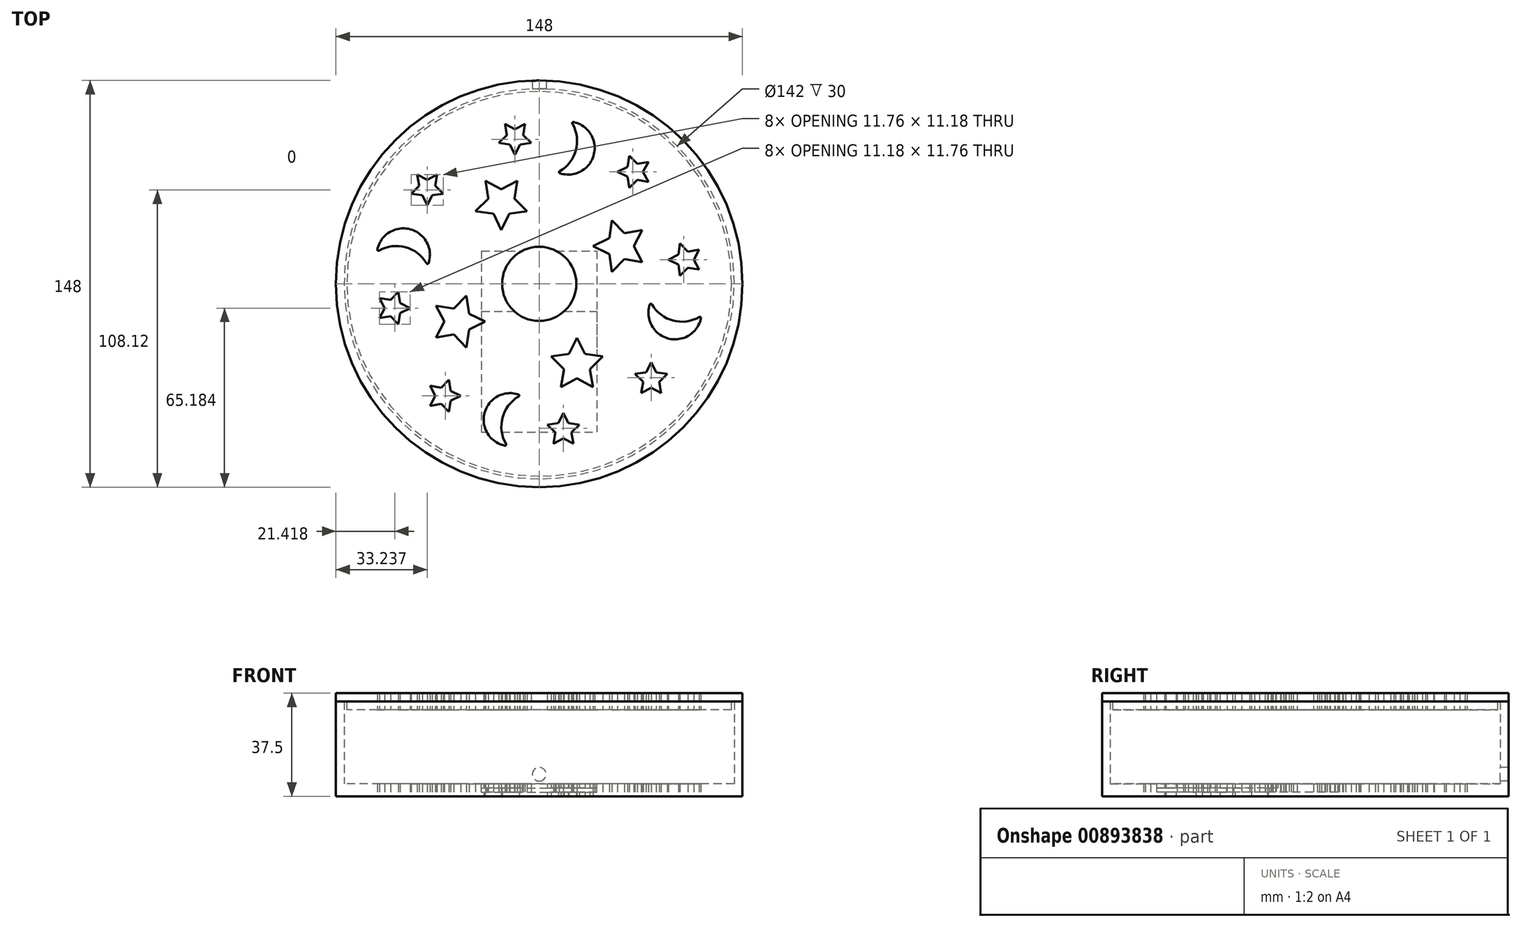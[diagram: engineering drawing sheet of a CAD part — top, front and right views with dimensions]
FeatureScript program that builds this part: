
annotation { "Feature Type Name" : "Feature", "Feature Type Description" : "" }
export const myFeature = defineFeature(function(context is Context, id is Id, definition is map)
    precondition{}
    {
        {
            assignVariable(context, id + "F0", {"name" : "BaseHeight", "anyValue" : 30});
        }
        {
            assignVariable(context, id + "F1", {"name" : "BaseThickness", "anyValue" : 4.5});
        }
        {
            assignVariable(context, id + "F2", {"name" : "CoverThickness", "anyValue" : 3});
        }
        {
            assignVariable(context, id + "F3", {"name" : "CoverLedge", "anyValue" : 3});
        }
        {
            var Q0;
            Q0=qCreatedBy(makeId("Top.planeOp"),FACE);
            var sketch = newSketch(context, id + "F4", { "sketchPlane" : qUnion([Q0])});
            skCircle(sketch, "E0", {"center": v(0, 0) * mm, "radius": 71 * mm});
            skCircle(sketch, "E1", {"center": v(0, 0) * mm, "radius": 74 * mm});
            skSolve(sketch);
        }
        {
            var Q0;
            Q0=makeQuery(id+"F4.imprint","IMPRINT",FACE,{"disambiguationData":[TD([[makeQuery(id+"F4.imprint","IMPRINT",EDGE,{"derivedFrom":sQuery(id+"F4.wireOp",EDGE,"E0")}),-1.0]])]});
            extrude(context, id + "F5", {"entities" : qUnion([Q0]), "depth" : (getVariable(context, 'BaseHeight') + getVariable(context, 'BaseThickness')) * mm, "offsetDistance" : 25 * mm});
        }
        {
            var Q0;
            Q0=makeQuery(id+"F4.imprint","IMPRINT",FACE,{"disambiguationData":[TD([[makeQuery(id+"F4.imprint","IMPRINT",EDGE,{"derivedFrom":sQuery(id+"F4.wireOp",EDGE,"E0")}),1.0]])]});
            extrude(context, id + "F6", {"entities" : qUnion([Q0]), "operationType" : NewBodyOperationType.ADD, "depth" : (getVariable(context, 'BaseThickness')) * mm, "offsetDistance" : 25 * mm});
        }
        {
            var Q0;
            Q0=qCreatedBy(makeId("Front.planeOp"),FACE);
            var sketch = newSketch(context, id + "F7", { "sketchPlane" : qUnion([Q0])});
            skLineSegment(sketch, "E2", {"start": v(0, 0) * mm, "end": v(0, 73.12) * mm, "construction": true});
            skSolve(sketch);
        }
        {
            var Q0;
            Q0=qCreatedBy(makeId("Front.planeOp"),FACE);
            var sketch = newSketch(context, id + "F8", { "sketchPlane" : qUnion([Q0])});
            skLineSegment(sketch, "E3.0.0", {"start": v(74, 0) * mm, "end": v(-74, 0) * mm});
            skLineSegment(sketch, "E4.0", {"start": v(-74, 34.5) * mm, "end": v(74, 34.5) * mm});
            skCircle(sketch, "E5", {"center": v(0, 8) * mm, "radius": 2.5 * mm});
            skSolve(sketch);
        }
        {
            var Q0;
            Q0=qSketchRegion(id+"F8",true);
            extrude(context, id + "F9", {"entities" : qUnion([Q0]), "operationType" : NewBodyOperationType.REMOVE, "endBound" : BoundingType.THROUGH_ALL, "oppositeDirection" : true, "depth" : 25 * mm, "offsetDistance" : 25 * mm});
        }
        {
            var Q0;
            Q0=qCreatedBy(makeId("Top.planeOp"),FACE);
            cPlane(context, id + "F10", {"entities" : qUnion([Q0]), "cplaneType" : CPlaneType.OFFSET, "offset" : (getVariable(context, 'BaseThickness')) * mm, "width" : 150 * mm, "height" : 150 * mm});
        }
        {
            var Q0;
            Q0=qCreatedBy(id+"F10.planeOp",FACE);
            var sketch = newSketch(context, id + "F11", { "sketchPlane" : qUnion([Q0])});
            skLineSegment(sketch, "E6.bottom", {"start": v(-21, 12) * mm, "end": v(21, 12) * mm});
            skLineSegment(sketch, "E6.top", {"start": v(-21, -54) * mm, "end": v(21, -54) * mm});
            skLineSegment(sketch, "E6.left", {"start": v(-21, 12) * mm, "end": v(-21, -54) * mm});
            skLineSegment(sketch, "E6.right", {"start": v(21, 12) * mm, "end": v(21, -54) * mm});
            skLineSegment(sketch, "E7", {"start": v(0, 35.82) * mm, "end": v(0, -36.35) * mm, "construction": true});
            skSolve(sketch);
        }
        {
            var Q0;
            Q0=qSketchRegion(id+"F11",true);
            extrude(context, id + "F12", {"entities" : qUnion([Q0]), "operationType" : NewBodyOperationType.REMOVE, "oppositeDirection" : true, "depth" : (getVariable(context, 'BaseThickness') - 1.5) * mm, "offsetDistance" : 25 * mm});
        }
        {
            var Q0;
            Q0=makeQuery(id+"F6.opExtrude","CAP_FACE",FACE,{"disambiguationData":[OSD([sQuery(id+"F4.wireOp",EDGE,"E0")])],"isStart":false});
            var sketch = newSketch(context, id + "F13", { "sketchPlane" : qUnion([Q0])});
            skLineSegment(sketch, "E8", {"start": v(-21, -10) * mm, "end": v(21, -10) * mm});
            skLineSegment(sketch, "E9", {"start": v(-21, -10) * mm, "end": v(-21, -54) * mm});
            skLineSegment(sketch, "E10", {"start": v(-21, -54) * mm, "end": v(21, -54) * mm});
            skLineSegment(sketch, "E11", {"start": v(21, -54) * mm, "end": v(21, -10) * mm});
            skSolve(sketch);
        }
        {
            var Q0;
            Q0=makeQuery(id+"F13.imprint","IMPRINT",FACE,{"disambiguationData":[TD([[makeQuery(id+"F13.imprint","IMPRINT",EDGE,{"derivedFrom":sQuery(id+"F13.wireOp",EDGE,"E8")}),-1.0]])]});
            extrude(context, id + "F14", {"entities" : qUnion([Q0]), "operationType" : NewBodyOperationType.ADD, "oppositeDirection" : true, "depth" : 1.5 * mm, "offsetDistance" : 25 * mm});
        }
        {
            var Q0;
            Q0=makeQuery(id+"F5.opExtrude","CAP_FACE",FACE,{"disambiguationData":[OSD([sQuery(id+"F4.wireOp",EDGE,"E0"),sQuery(id+"F4.wireOp",EDGE,"E1")])],"isStart":false});
            cPlane(context, id + "F15", {"entities" : qUnion([Q0]), "cplaneType" : CPlaneType.OFFSET, "offset" : 0 * mm, "width" : 150 * mm, "height" : 150 * mm});
        }
        {
            var Q0;
            Q0=qCreatedBy(id+"F15.planeOp",FACE);
            var sketch = newSketch(context, id + "F16", { "sketchPlane" : qUnion([Q0])});
            skCircle(sketch, "E12.0", {"center": v(0, 0) * mm, "radius": 74 * mm});
            skCircle(sketch, "E13.0", {"center": v(0, 0) * mm, "radius": 71 * mm});
            skCircle(sketch, "E14.0", {"center": v(0, 0) * mm, "radius": 70 * mm});
            skCircle(sketch, "E15.0", {"center": v(0, 0) * mm, "radius": 67 * mm});
            skSolve(sketch);
        }
        {
            var Q0;
            Q0=qSketchRegion(id+"F16",true);
            var Q1;
            Q1=makeQuery(id+"F16.imprint","IMPRINT",FACE,{"disambiguationData":[TD([[makeQuery(id+"F16.imprint","IMPRINT",EDGE,{"derivedFrom":sQuery(id+"F16.wireOp",EDGE,"E13.0")}),1.0]])]});
            var Q2;
            Q2=makeQuery(id+"F16.imprint","IMPRINT",FACE,{"disambiguationData":[TD([[makeQuery(id+"F16.imprint","IMPRINT",EDGE,{"derivedFrom":sQuery(id+"F16.wireOp",EDGE,"E14.0")}),1.0]])]});
            var Q3;
            Q3=makeQuery(id+"F16.imprint","IMPRINT",FACE,{"disambiguationData":[TD([[makeQuery(id+"F16.imprint","IMPRINT",EDGE,{"derivedFrom":sQuery(id+"F16.wireOp",EDGE,"E15.0")}),1.0]])]});
            extrude(context, id + "F17", {"entities" : qUnion([Q0, Q1, Q2, Q3]), "depth" : (getVariable(context, 'CoverThickness')) * mm, "offsetDistance" : 25 * mm});
        }
        {
            var Q0;
            Q0=makeQuery(id+"F16.imprint","IMPRINT",FACE,{"disambiguationData":[TD([[makeQuery(id+"F16.imprint","IMPRINT",EDGE,{"derivedFrom":sQuery(id+"F16.wireOp",EDGE,"E14.0")}),1.0]])]});
            var Q1;
            Q1=makeQuery(id+"F16.imprint","IMPRINT",FACE,{"disambiguationData":[TD([[makeQuery(id+"F16.imprint","IMPRINT",EDGE,{"derivedFrom":sQuery(id+"F16.wireOp",EDGE,"E15.0")}),1.0]])]});
            extrude(context, id + "F18", {"entities" : qUnion([Q0, Q1]), "operationType" : NewBodyOperationType.ADD, "oppositeDirection" : true, "depth" : (getVariable(context, 'CoverLedge')) * mm, "offsetDistance" : 25 * mm});
        }
        {
            var Q0;
            Q0=qCreatedBy(id+"F15.planeOp",FACE);
            var sketch = newSketch(context, id + "F19", { "sketchPlane" : qUnion([Q0])});
            skCircle(sketch, "E16", {"center": v(0, 0) * mm, "radius": 13.5 * mm});
            skPoint(sketch, "E17", {"position": v(34.71, 40.76) * mm});
            skLineSegment(sketch, "E18", {"start": v(28.53, 40.76) * mm, "end": v(32.21, 42.58) * mm});
            skLineSegment(sketch, "E19", {"start": v(32.21, 42.58) * mm, "end": v(32.8, 46.64) * mm});
            skLineSegment(sketch, "E20", {"start": v(32.8, 46.64) * mm, "end": v(35.67, 43.7) * mm});
            skLineSegment(sketch, "E21", {"start": v(35.67, 43.7) * mm, "end": v(39.71, 44.4) * mm});
            skLineSegment(sketch, "E22", {"start": v(39.71, 44.4) * mm, "end": v(37.8, 40.76) * mm});
            skLineSegment(sketch, "E23", {"start": v(37.8, 40.76) * mm, "end": v(39.71, 37.13) * mm});
            skLineSegment(sketch, "E24", {"start": v(39.71, 37.13) * mm, "end": v(35.67, 37.82) * mm});
            skLineSegment(sketch, "E25", {"start": v(35.67, 37.82) * mm, "end": v(32.8, 34.89) * mm});
            skLineSegment(sketch, "E26", {"start": v(32.8, 34.89) * mm, "end": v(32.21, 38.95) * mm});
            skLineSegment(sketch, "E27", {"start": v(32.21, 38.95) * mm, "end": v(28.53, 40.76) * mm});
            skPoint(sketch, "E28", {"position": v(53.17, 8.82) * mm});
            skLineSegment(sketch, "E29", {"start": v(47, 8.82) * mm, "end": v(50.67, 10.63) * mm});
            skLineSegment(sketch, "E30", {"start": v(50.67, 10.63) * mm, "end": v(51.26, 14.7) * mm});
            skLineSegment(sketch, "E31", {"start": v(51.26, 14.7) * mm, "end": v(54.13, 11.76) * mm});
            skLineSegment(sketch, "E32", {"start": v(54.13, 11.76) * mm, "end": v(58.17, 12.45) * mm});
            skLineSegment(sketch, "E33", {"start": v(58.17, 12.45) * mm, "end": v(56.26, 8.82) * mm});
            skLineSegment(sketch, "E34", {"start": v(56.26, 8.82) * mm, "end": v(58.17, 5.18) * mm});
            skLineSegment(sketch, "E35", {"start": v(58.17, 5.18) * mm, "end": v(54.13, 5.88) * mm});
            skLineSegment(sketch, "E36", {"start": v(54.13, 5.88) * mm, "end": v(51.26, 2.94) * mm});
            skLineSegment(sketch, "E37", {"start": v(51.26, 2.94) * mm, "end": v(50.67, 7) * mm});
            skLineSegment(sketch, "E38", {"start": v(50.67, 7) * mm, "end": v(47, 8.82) * mm});
            skLineSegment(sketch, "E39", {"start": v(19.63, 13.76) * mm, "end": v(25.52, 16.67) * mm});
            skLineSegment(sketch, "E40", {"start": v(25.52, 16.67) * mm, "end": v(26.46, 23.16) * mm});
            skLineSegment(sketch, "E41", {"start": v(26.46, 23.16) * mm, "end": v(31.05, 18.46) * mm});
            skLineSegment(sketch, "E42", {"start": v(31.05, 18.46) * mm, "end": v(37.52, 19.57) * mm});
            skLineSegment(sketch, "E43", {"start": v(37.52, 19.57) * mm, "end": v(34.46, 13.76) * mm});
            skLineSegment(sketch, "E44", {"start": v(34.46, 13.76) * mm, "end": v(37.52, 7.95) * mm});
            skLineSegment(sketch, "E45", {"start": v(37.52, 7.95) * mm, "end": v(31.05, 9.06) * mm});
            skLineSegment(sketch, "E46", {"start": v(31.05, 9.06) * mm, "end": v(26.46, 4.35) * mm});
            skLineSegment(sketch, "E47", {"start": v(26.46, 4.35) * mm, "end": v(25.52, 10.85) * mm});
            skLineSegment(sketch, "E48", {"start": v(25.52, 10.85) * mm, "end": v(19.63, 13.76) * mm});
            skArc(sketch, "E49", {"start": v(7.54, 40.26) * mm, "mid": v(19.88, 46.94) * mm, "end": v(12.5, 58.88) * mm});
            skArc(sketch, "E50", {"start": v(7.46, 41) * mm, "mid": v(13.35, 48.68) * mm, "end": v(12.08, 58.29) * mm});
            skPoint(sketch, "E51.visualSharp", {"position": v(11.62, 59.02) * mm});
            skArc(sketch, "E51.filletArc", {"start": v(12.5, 58.88) * mm, "mid": v(12.1, 58.72) * mm, "end": v(12.08, 58.29) * mm});
            skPoint(sketch, "E52.visualSharp", {"position": v(6.7, 40.58) * mm});
            skArc(sketch, "E52.filletArc", {"start": v(7.46, 41) * mm, "mid": v(7.27, 40.6) * mm, "end": v(7.54, 40.26) * mm});
            skArc(sketch, "E53.1.0", {"start": v(-40.26, 7.54) * mm, "mid": v(-46.94, 19.88) * mm, "end": v(-58.88, 12.5) * mm});
            skArc(sketch, "E53.1.1", {"start": v(-41, 7.46) * mm, "mid": v(-48.68, 13.35) * mm, "end": v(-58.29, 12.08) * mm});
            skLineSegment(sketch, "E53.1.2", {"start": v(-44.4, 39.71) * mm, "end": v(-40.76, 37.8) * mm});
            skPoint(sketch, "E53.1.3", {"position": v(-40.76, 34.71) * mm});
            skLineSegment(sketch, "E53.1.4", {"start": v(-46.64, 32.8) * mm, "end": v(-43.7, 35.67) * mm});
            skLineSegment(sketch, "E53.1.5", {"start": v(-37.13, 39.71) * mm, "end": v(-37.82, 35.67) * mm});
            skLineSegment(sketch, "E53.1.6", {"start": v(-38.95, 32.21) * mm, "end": v(-40.76, 28.53) * mm});
            skLineSegment(sketch, "E53.1.7", {"start": v(-37.82, 35.67) * mm, "end": v(-34.89, 32.8) * mm});
            skLineSegment(sketch, "E53.1.8", {"start": v(-40.76, 37.8) * mm, "end": v(-37.13, 39.71) * mm});
            skLineSegment(sketch, "E53.1.9", {"start": v(-42.58, 32.21) * mm, "end": v(-46.64, 32.8) * mm});
            skLineSegment(sketch, "E53.1.10", {"start": v(-43.7, 35.67) * mm, "end": v(-44.4, 39.71) * mm});
            skLineSegment(sketch, "E53.1.11", {"start": v(-40.76, 28.53) * mm, "end": v(-42.58, 32.21) * mm});
            skLineSegment(sketch, "E53.1.12", {"start": v(-34.89, 32.8) * mm, "end": v(-38.95, 32.21) * mm});
            skPoint(sketch, "E53.1.13", {"position": v(-8.82, 53.17) * mm});
            skLineSegment(sketch, "E53.1.14", {"start": v(-8.82, 56.26) * mm, "end": v(-5.18, 58.17) * mm});
            skLineSegment(sketch, "E53.1.15", {"start": v(-11.76, 54.13) * mm, "end": v(-12.45, 58.17) * mm});
            skLineSegment(sketch, "E53.1.16", {"start": v(-5.18, 58.17) * mm, "end": v(-5.88, 54.13) * mm});
            skLineSegment(sketch, "E53.1.17", {"start": v(-12.45, 58.17) * mm, "end": v(-8.82, 56.26) * mm});
            skLineSegment(sketch, "E53.1.18", {"start": v(-14.7, 51.26) * mm, "end": v(-11.76, 54.13) * mm});
            skLineSegment(sketch, "E53.1.19", {"start": v(-7, 50.67) * mm, "end": v(-8.82, 47) * mm});
            skLineSegment(sketch, "E53.1.20", {"start": v(-2.94, 51.26) * mm, "end": v(-7, 50.67) * mm});
            skLineSegment(sketch, "E53.1.21", {"start": v(-8.82, 47) * mm, "end": v(-10.63, 50.67) * mm});
            skLineSegment(sketch, "E53.1.22", {"start": v(-5.88, 54.13) * mm, "end": v(-2.94, 51.26) * mm});
            skLineSegment(sketch, "E53.1.23", {"start": v(-10.63, 50.67) * mm, "end": v(-14.7, 51.26) * mm});
            skLineSegment(sketch, "E53.1.24", {"start": v(-23.16, 26.46) * mm, "end": v(-18.46, 31.05) * mm});
            skLineSegment(sketch, "E53.1.25", {"start": v(-9.06, 31.05) * mm, "end": v(-4.35, 26.46) * mm});
            skLineSegment(sketch, "E53.1.26", {"start": v(-10.85, 25.52) * mm, "end": v(-13.76, 19.63) * mm});
            skLineSegment(sketch, "E53.1.27", {"start": v(-7.95, 37.52) * mm, "end": v(-9.06, 31.05) * mm});
            skLineSegment(sketch, "E53.1.28", {"start": v(-16.67, 25.52) * mm, "end": v(-23.16, 26.46) * mm});
            skLineSegment(sketch, "E53.1.29", {"start": v(-13.76, 34.46) * mm, "end": v(-7.95, 37.52) * mm});
            skLineSegment(sketch, "E53.1.30", {"start": v(-13.76, 19.63) * mm, "end": v(-16.67, 25.52) * mm});
            skLineSegment(sketch, "E53.1.31", {"start": v(-18.46, 31.05) * mm, "end": v(-19.57, 37.52) * mm});
            skLineSegment(sketch, "E53.1.32", {"start": v(-4.35, 26.46) * mm, "end": v(-10.85, 25.52) * mm});
            skLineSegment(sketch, "E53.1.33", {"start": v(-19.57, 37.52) * mm, "end": v(-13.76, 34.46) * mm});
            skArc(sketch, "E53.2.0", {"start": v(-7.54, -40.26) * mm, "mid": v(-19.88, -46.94) * mm, "end": v(-12.5, -58.88) * mm});
            skArc(sketch, "E53.2.1", {"start": v(-7.46, -41) * mm, "mid": v(-13.35, -48.68) * mm, "end": v(-12.08, -58.29) * mm});
            skLineSegment(sketch, "E53.2.2", {"start": v(-39.71, -44.4) * mm, "end": v(-37.8, -40.76) * mm});
            skPoint(sketch, "E53.2.3", {"position": v(-34.71, -40.76) * mm});
            skLineSegment(sketch, "E53.2.4", {"start": v(-32.8, -46.64) * mm, "end": v(-35.67, -43.7) * mm});
            skLineSegment(sketch, "E53.2.5", {"start": v(-39.71, -37.13) * mm, "end": v(-35.67, -37.82) * mm});
            skLineSegment(sketch, "E53.2.6", {"start": v(-32.21, -38.95) * mm, "end": v(-28.53, -40.76) * mm});
            skLineSegment(sketch, "E53.2.7", {"start": v(-35.67, -37.82) * mm, "end": v(-32.8, -34.89) * mm});
            skLineSegment(sketch, "E53.2.8", {"start": v(-37.8, -40.76) * mm, "end": v(-39.71, -37.13) * mm});
            skLineSegment(sketch, "E53.2.9", {"start": v(-32.21, -42.58) * mm, "end": v(-32.8, -46.64) * mm});
            skLineSegment(sketch, "E53.2.10", {"start": v(-35.67, -43.7) * mm, "end": v(-39.71, -44.4) * mm});
            skLineSegment(sketch, "E53.2.11", {"start": v(-28.53, -40.76) * mm, "end": v(-32.21, -42.58) * mm});
            skLineSegment(sketch, "E53.2.12", {"start": v(-32.8, -34.89) * mm, "end": v(-32.21, -38.95) * mm});
            skPoint(sketch, "E53.2.13", {"position": v(-53.17, -8.82) * mm});
            skLineSegment(sketch, "E53.2.14", {"start": v(-56.26, -8.82) * mm, "end": v(-58.17, -5.18) * mm});
            skLineSegment(sketch, "E53.2.15", {"start": v(-54.13, -11.76) * mm, "end": v(-58.17, -12.45) * mm});
            skLineSegment(sketch, "E53.2.16", {"start": v(-58.17, -5.18) * mm, "end": v(-54.13, -5.88) * mm});
            skLineSegment(sketch, "E53.2.17", {"start": v(-58.17, -12.45) * mm, "end": v(-56.26, -8.82) * mm});
            skLineSegment(sketch, "E53.2.18", {"start": v(-51.26, -14.7) * mm, "end": v(-54.13, -11.76) * mm});
            skLineSegment(sketch, "E53.2.19", {"start": v(-50.67, -7) * mm, "end": v(-47, -8.82) * mm});
            skLineSegment(sketch, "E53.2.20", {"start": v(-51.26, -2.94) * mm, "end": v(-50.67, -7) * mm});
            skLineSegment(sketch, "E53.2.21", {"start": v(-47, -8.82) * mm, "end": v(-50.67, -10.63) * mm});
            skLineSegment(sketch, "E53.2.22", {"start": v(-54.13, -5.88) * mm, "end": v(-51.26, -2.94) * mm});
            skLineSegment(sketch, "E53.2.23", {"start": v(-50.67, -10.63) * mm, "end": v(-51.26, -14.7) * mm});
            skLineSegment(sketch, "E53.2.24", {"start": v(-26.46, -23.16) * mm, "end": v(-31.05, -18.46) * mm});
            skLineSegment(sketch, "E53.2.25", {"start": v(-31.05, -9.06) * mm, "end": v(-26.46, -4.35) * mm});
            skLineSegment(sketch, "E53.2.26", {"start": v(-25.52, -10.85) * mm, "end": v(-19.63, -13.76) * mm});
            skLineSegment(sketch, "E53.2.27", {"start": v(-37.52, -7.95) * mm, "end": v(-31.05, -9.06) * mm});
            skLineSegment(sketch, "E53.2.28", {"start": v(-25.52, -16.67) * mm, "end": v(-26.46, -23.16) * mm});
            skLineSegment(sketch, "E53.2.29", {"start": v(-34.46, -13.76) * mm, "end": v(-37.52, -7.95) * mm});
            skLineSegment(sketch, "E53.2.30", {"start": v(-19.63, -13.76) * mm, "end": v(-25.52, -16.67) * mm});
            skLineSegment(sketch, "E53.2.31", {"start": v(-31.05, -18.46) * mm, "end": v(-37.52, -19.57) * mm});
            skLineSegment(sketch, "E53.2.32", {"start": v(-26.46, -4.35) * mm, "end": v(-25.52, -10.85) * mm});
            skLineSegment(sketch, "E53.2.33", {"start": v(-37.52, -19.57) * mm, "end": v(-34.46, -13.76) * mm});
            skArc(sketch, "E53.3.0", {"start": v(40.26, -7.54) * mm, "mid": v(46.94, -19.88) * mm, "end": v(58.88, -12.5) * mm});
            skArc(sketch, "E53.3.1", {"start": v(41, -7.46) * mm, "mid": v(48.68, -13.35) * mm, "end": v(58.29, -12.08) * mm});
            skLineSegment(sketch, "E53.3.2", {"start": v(44.4, -39.71) * mm, "end": v(40.76, -37.8) * mm});
            skPoint(sketch, "E53.3.3", {"position": v(40.76, -34.71) * mm});
            skLineSegment(sketch, "E53.3.4", {"start": v(46.64, -32.8) * mm, "end": v(43.7, -35.67) * mm});
            skLineSegment(sketch, "E53.3.5", {"start": v(37.13, -39.71) * mm, "end": v(37.82, -35.67) * mm});
            skLineSegment(sketch, "E53.3.6", {"start": v(38.95, -32.21) * mm, "end": v(40.76, -28.53) * mm});
            skLineSegment(sketch, "E53.3.7", {"start": v(37.82, -35.67) * mm, "end": v(34.89, -32.8) * mm});
            skLineSegment(sketch, "E53.3.8", {"start": v(40.76, -37.8) * mm, "end": v(37.13, -39.71) * mm});
            skLineSegment(sketch, "E53.3.9", {"start": v(42.58, -32.21) * mm, "end": v(46.64, -32.8) * mm});
            skLineSegment(sketch, "E53.3.10", {"start": v(43.7, -35.67) * mm, "end": v(44.4, -39.71) * mm});
            skLineSegment(sketch, "E53.3.11", {"start": v(40.76, -28.53) * mm, "end": v(42.58, -32.21) * mm});
            skLineSegment(sketch, "E53.3.12", {"start": v(34.89, -32.8) * mm, "end": v(38.95, -32.21) * mm});
            skPoint(sketch, "E53.3.13", {"position": v(8.82, -53.17) * mm});
            skLineSegment(sketch, "E53.3.14", {"start": v(8.82, -56.26) * mm, "end": v(5.18, -58.17) * mm});
            skLineSegment(sketch, "E53.3.15", {"start": v(11.76, -54.13) * mm, "end": v(12.45, -58.17) * mm});
            skLineSegment(sketch, "E53.3.16", {"start": v(5.18, -58.17) * mm, "end": v(5.88, -54.13) * mm});
            skLineSegment(sketch, "E53.3.17", {"start": v(12.45, -58.17) * mm, "end": v(8.82, -56.26) * mm});
            skLineSegment(sketch, "E53.3.18", {"start": v(14.7, -51.26) * mm, "end": v(11.76, -54.13) * mm});
            skLineSegment(sketch, "E53.3.19", {"start": v(7, -50.67) * mm, "end": v(8.82, -47) * mm});
            skLineSegment(sketch, "E53.3.20", {"start": v(2.94, -51.26) * mm, "end": v(7, -50.67) * mm});
            skLineSegment(sketch, "E53.3.21", {"start": v(8.82, -47) * mm, "end": v(10.63, -50.67) * mm});
            skLineSegment(sketch, "E53.3.22", {"start": v(5.88, -54.13) * mm, "end": v(2.94, -51.26) * mm});
            skLineSegment(sketch, "E53.3.23", {"start": v(10.63, -50.67) * mm, "end": v(14.7, -51.26) * mm});
            skLineSegment(sketch, "E53.3.24", {"start": v(23.16, -26.46) * mm, "end": v(18.46, -31.05) * mm});
            skLineSegment(sketch, "E53.3.25", {"start": v(9.06, -31.05) * mm, "end": v(4.35, -26.46) * mm});
            skLineSegment(sketch, "E53.3.26", {"start": v(10.85, -25.52) * mm, "end": v(13.76, -19.63) * mm});
            skLineSegment(sketch, "E53.3.27", {"start": v(7.95, -37.52) * mm, "end": v(9.06, -31.05) * mm});
            skLineSegment(sketch, "E53.3.28", {"start": v(16.67, -25.52) * mm, "end": v(23.16, -26.46) * mm});
            skLineSegment(sketch, "E53.3.29", {"start": v(13.76, -34.46) * mm, "end": v(7.95, -37.52) * mm});
            skLineSegment(sketch, "E53.3.30", {"start": v(13.76, -19.63) * mm, "end": v(16.67, -25.52) * mm});
            skLineSegment(sketch, "E53.3.31", {"start": v(18.46, -31.05) * mm, "end": v(19.57, -37.52) * mm});
            skLineSegment(sketch, "E53.3.32", {"start": v(4.35, -26.46) * mm, "end": v(10.85, -25.52) * mm});
            skLineSegment(sketch, "E53.3.33", {"start": v(19.57, -37.52) * mm, "end": v(13.76, -34.46) * mm});
            skArc(sketch, "E54.1.0", {"start": v(-41, 7.46) * mm, "mid": v(-40.6, 7.27) * mm, "end": v(-40.26, 7.54) * mm});
            skArc(sketch, "E54.1.1", {"start": v(-58.88, 12.5) * mm, "mid": v(-58.72, 12.1) * mm, "end": v(-58.29, 12.08) * mm});
            skArc(sketch, "E54.2.0", {"start": v(-7.46, -41) * mm, "mid": v(-7.27, -40.6) * mm, "end": v(-7.54, -40.26) * mm});
            skArc(sketch, "E54.2.1", {"start": v(-12.5, -58.88) * mm, "mid": v(-12.1, -58.72) * mm, "end": v(-12.08, -58.29) * mm});
            skArc(sketch, "E54.3.0", {"start": v(41, -7.46) * mm, "mid": v(40.6, -7.27) * mm, "end": v(40.26, -7.54) * mm});
            skArc(sketch, "E54.3.1", {"start": v(58.88, -12.5) * mm, "mid": v(58.72, -12.1) * mm, "end": v(58.29, -12.08) * mm});
            skSolve(sketch);
        }
        {
            var Q0;
            Q0=makeQuery(id+"F19.imprint","IMPRINT",FACE,{"disambiguationData":[TD([[makeQuery(id+"F19.imprint","IMPRINT",EDGE,{"derivedFrom":sQuery(id+"F19.wireOp",EDGE,"E39")}),-1.0]])]});
            var Q1;
            Q1=makeQuery(id+"F19.imprint","IMPRINT",FACE,{"disambiguationData":[TD([[makeQuery(id+"F19.imprint","IMPRINT",EDGE,{"derivedFrom":sQuery(id+"F19.wireOp",EDGE,"E29")}),-1.0]])]});
            var Q2;
            Q2=makeQuery(id+"F19.imprint","IMPRINT",FACE,{"disambiguationData":[TD([[makeQuery(id+"F19.imprint","IMPRINT",EDGE,{"derivedFrom":sQuery(id+"F19.wireOp",EDGE,"E18")}),-1.0]])]});
            var Q3;
            Q3=makeQuery(id+"F19.imprint","IMPRINT",FACE,{"disambiguationData":[TD([[makeQuery(id+"F19.imprint","IMPRINT",EDGE,{"derivedFrom":sQuery(id+"F19.wireOp",EDGE,"E49")}),1.0]])]});
            var Q4;
            Q4=makeQuery(id+"F19.imprint","IMPRINT",FACE,{"disambiguationData":[TD([[makeQuery(id+"F19.imprint","IMPRINT",EDGE,{"derivedFrom":sQuery(id+"F19.wireOp",EDGE,"E16")}),1.0]])]});
            var Q5;
            Q5=makeQuery(id+"F19.imprint","IMPRINT",FACE,{"disambiguationData":[TD([[makeQuery(id+"F19.imprint","IMPRINT",EDGE,{"derivedFrom":sQuery(id+"F19.wireOp",EDGE,"E53.2.24")}),-1.0]])]});
            var Q6;
            Q6=makeQuery(id+"F19.imprint","IMPRINT",FACE,{"disambiguationData":[TD([[makeQuery(id+"F19.imprint","IMPRINT",EDGE,{"derivedFrom":sQuery(id+"F19.wireOp",EDGE,"E53.1.24")}),-1.0]])]});
            var Q7;
            Q7=makeQuery(id+"F19.imprint","IMPRINT",FACE,{"disambiguationData":[TD([[makeQuery(id+"F19.imprint","IMPRINT",EDGE,{"derivedFrom":sQuery(id+"F19.wireOp",EDGE,"E53.1.14")}),-1.0]])]});
            var Q8;
            Q8=makeQuery(id+"F19.imprint","IMPRINT",FACE,{"disambiguationData":[TD([[makeQuery(id+"F19.imprint","IMPRINT",EDGE,{"derivedFrom":sQuery(id+"F19.wireOp",EDGE,"E53.1.2")}),-1.0]])]});
            var Q9;
            Q9=makeQuery(id+"F19.imprint","IMPRINT",FACE,{"disambiguationData":[TD([[makeQuery(id+"F19.imprint","IMPRINT",EDGE,{"derivedFrom":sQuery(id+"F19.wireOp",EDGE,"E53.3.14")}),-1.0]])]});
            var Q10;
            Q10=makeQuery(id+"F19.imprint","IMPRINT",FACE,{"disambiguationData":[TD([[makeQuery(id+"F19.imprint","IMPRINT",EDGE,{"derivedFrom":sQuery(id+"F19.wireOp",EDGE,"E53.3.2")}),-1.0]])]});
            var Q11;
            Q11=makeQuery(id+"F19.imprint","IMPRINT",FACE,{"disambiguationData":[TD([[makeQuery(id+"F19.imprint","IMPRINT",EDGE,{"derivedFrom":sQuery(id+"F19.wireOp",EDGE,"E53.2.2")}),-1.0]])]});
            var Q12;
            Q12=makeQuery(id+"F19.imprint","IMPRINT",FACE,{"disambiguationData":[TD([[makeQuery(id+"F19.imprint","IMPRINT",EDGE,{"derivedFrom":sQuery(id+"F19.wireOp",EDGE,"E53.2.14")}),-1.0]])]});
            var Q13;
            Q13=makeQuery(id+"F19.imprint","IMPRINT",FACE,{"disambiguationData":[TD([[makeQuery(id+"F19.imprint","IMPRINT",EDGE,{"derivedFrom":sQuery(id+"F19.wireOp",EDGE,"E53.2.0")}),1.0]])]});
            var Q14;
            Q14=makeQuery(id+"F19.imprint","IMPRINT",FACE,{"disambiguationData":[TD([[makeQuery(id+"F19.imprint","IMPRINT",EDGE,{"derivedFrom":sQuery(id+"F19.wireOp",EDGE,"E53.3.0")}),1.0]])]});
            var Q15;
            Q15=makeQuery(id+"F19.imprint","IMPRINT",FACE,{"disambiguationData":[TD([[makeQuery(id+"F19.imprint","IMPRINT",EDGE,{"derivedFrom":sQuery(id+"F19.wireOp",EDGE,"E53.3.24")}),-1.0]])]});
            var Q16;
            Q16=makeQuery(id+"F19.imprint","IMPRINT",FACE,{"disambiguationData":[TD([[makeQuery(id+"F19.imprint","IMPRINT",EDGE,{"derivedFrom":sQuery(id+"F19.wireOp",EDGE,"E53.1.0")}),1.0]])]});
            var Q17;
            Q17=makeQuery(id+"F17.opExtrude","CAP_FACE",FACE,{"disambiguationData":[OSD([sQuery(id+"F16.wireOp",EDGE,"E12.0")])],"isStart":false});
            extrude(context, id + "F20", {"entities" : qUnion([Q0, Q1, Q2, Q3, Q4, Q5, Q6, Q7, Q8, Q9, Q10, Q11, Q12, Q13, Q14, Q15, Q16]), "operationType" : NewBodyOperationType.REMOVE, "endBound" : BoundingType.THROUGH_ALL, "depth" : 5 * mm, "endBoundEntityFace" : qUnion([Q17]), "offsetDistance" : 25 * mm, "hasSecondDirection" : true, "secondDirectionBound" : BoundingType.THROUGH_ALL, "secondDirectionOppositeDirection" : true, "secondDirectionDepth" : 5 * mm});
        }
    });
